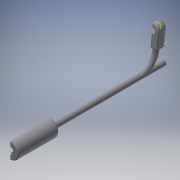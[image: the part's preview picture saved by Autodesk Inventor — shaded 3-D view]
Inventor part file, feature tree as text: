
AUTODESK INVENTOR PART (.ipt)
format: ipt  version: 2018 (Build 220112000, 112)  size: 426,496 bytes
history: native  units: mm
features: sketch x10, extrude x8, fillet x6, plane x3, projected_geometry x3, revolve x1, sweep x1
ambient origin geometry x8: Origin, YZ Plane, XZ Plane, XY Plane, X Axis, Y Axis, Z Axis, Center Point
bodies: Solid1 (feature_tree)
feature tree (32):
  revolve  "Revolution1"  [1 undecoded]
  fillet  "Fillet1"  Radius=8.0mm
  fillet  "Fillet2"  Radius=40.0mm
  fillet  "Fillet3"  [1 undecoded]
  plane  "Work Plane1"
  sweep  "Sweep1"
  extrude  "Extrusion2"  Depth=1.0mm
  fillet  "Fillet4"  Radius=1.0mm
  fillet  "Fillet5"  Radius=1.0mm
  extrude  "Extrusion3"  Depth=1.0mm
  extrude  "Extrusion4"  Depth=6.601018mm
  extrude  "Extrusion5"  Depth=1.0mm
  extrude  "Extrusion6"  [1 undecoded]
  extrude  "Extrusion7"  Depth=18.0mm
  plane  "Work Plane3"
  extrude  "Extrusion8"  TaperAngle=0.0deg  [1 undecoded]
  plane  "Work Plane5"
  extrude  "Extrusion9"  Depth=5.0mm
  fillet  "Fillet6"  Radius=6.0mm
  sketch  "Sketch6"  dims[d0=150.0mm d1=3.0mm d3=8.0mm d4=40.0mm d5=90.0deg]
  sketch  "Sketch8"  dims[d20=1.5mm d21=1.5mm]
  sketch  "Sketch9"  dims[d22=1.5mm d23=1.0mm d24=1.0mm d25=1.0mm]
  projected_geometry  "Projected Loop3"
  sketch  "Sketch10"  dims[d26=1.0mm d27=1.0mm]
  projected_geometry  "Projected Loop4"
  sketch  "Sketch11"  dims[d28=1.456552mm d29=6.601018mm]
  sketch  "Sketch12"  dims[d30=2.0mm d31=1.0mm]
  sketch  "Sketch13"  dims[d32=1.0mm d33=-23.0mm]
  sketch  "Sketch14"  dims[d38=18.0mm d39=18.0mm]
  sketch  "Sketch15"  dims[d40=16.0mm d41=0.0mm d42=0.0mm]
  projected_geometry  "Projected Loop5"
  sketch  "Sketch16"  dims[d43=12.0mm d44=5.0mm d45=6.0mm d46=6.0mm d47=20.0mm d48=0.0mm d49=6.0mm d50=1.0mm d51=3.0mm d52=5.5mm d53=8.0mm d54=0.0mm d55=10.0mm d56=0.0mm d57=50.0mm d58=0.0mm d59=1.4mm d60=0.0mm d61=4.332171mm d62=15.0mm d63=0.0mm d64=-3.0mm d65=6.5mm d66=1.1mm d67=0.0mm d68=-3.0mm d69=10.0mm d70=0.0mm d71=0.5mm d72=6.0mm]
note: 4 required parameter values undecoded (feature->parameter linkage not recoverable at this tier; creation-order binding heuristic only, values carry confidence <= 0.55)